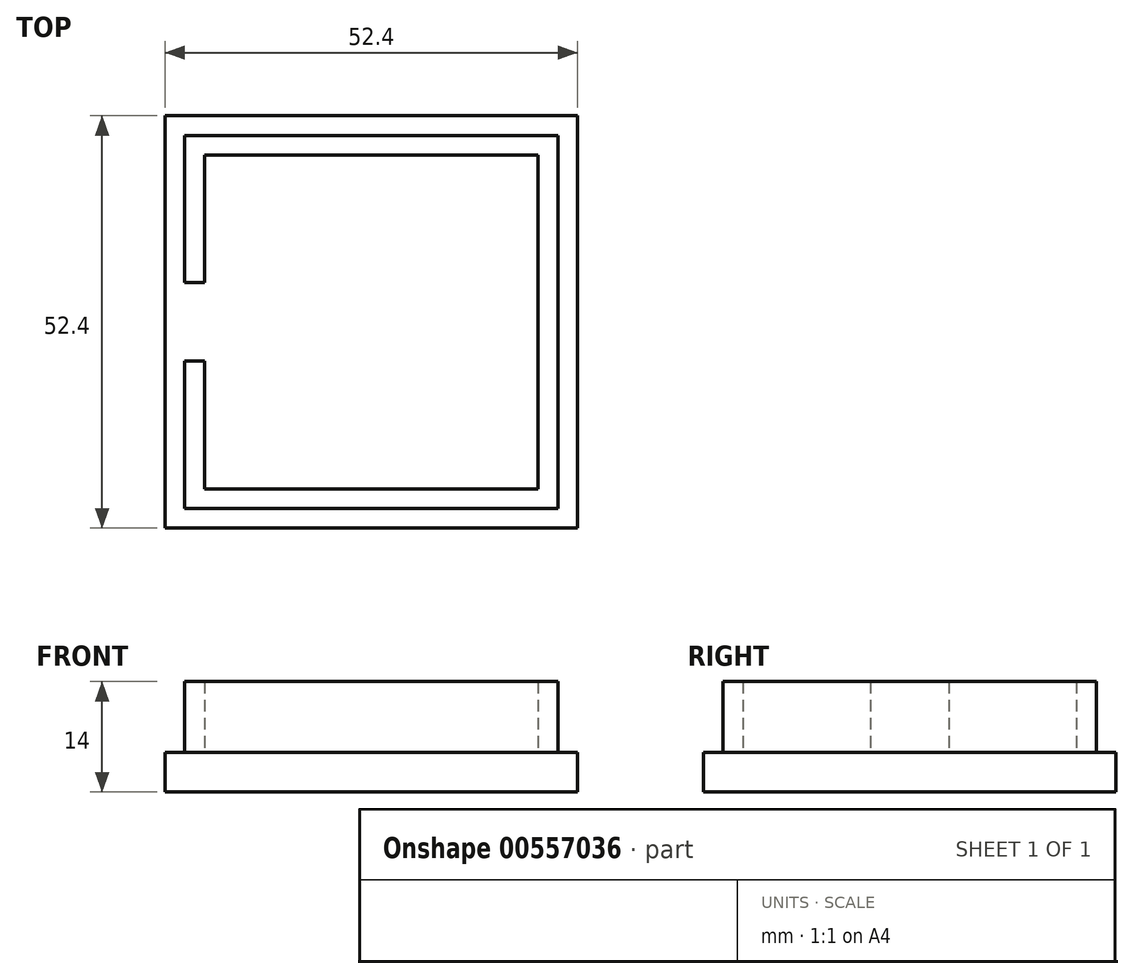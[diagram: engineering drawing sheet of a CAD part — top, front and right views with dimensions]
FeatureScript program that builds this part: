
annotation { "Feature Type Name" : "Feature", "Feature Type Description" : "" }
export const myFeature = defineFeature(function(context is Context, id is Id, definition is map)
    precondition{}
    {
        {
            var Q0;
            Q0=qCreatedBy(makeId("Top.planeOp"),FACE);
            var sketch = newSketch(context, id + "F0", { "sketchPlane" : qUnion([Q0])});
            skLineSegment(sketch, "E0.bottom", {"start": v(21.2, 21.2) * mm, "end": v(-21.2, 21.2) * mm});
            skLineSegment(sketch, "E0.top", {"start": v(21.2, -21.2) * mm, "end": v(-21.2, -21.2) * mm});
            skLineSegment(sketch, "E0.left", {"start": v(21.2, 21.2) * mm, "end": v(21.2, -21.2) * mm});
            skLineSegment(sketch, "E0.right", {"start": v(-21.2, 21.2) * mm, "end": v(-21.2, -21.2) * mm});
            skPoint(sketch, "E0.middle", {"position": v(0, 0) * mm});
            skLineSegment(sketch, "E1.bottom", {"start": v(23.7, 23.7) * mm, "end": v(-23.7, 23.7) * mm});
            skLineSegment(sketch, "E1.top", {"start": v(23.7, -23.7) * mm, "end": v(-23.7, -23.7) * mm});
            skLineSegment(sketch, "E1.left", {"start": v(23.7, 23.7) * mm, "end": v(23.7, -23.7) * mm});
            skLineSegment(sketch, "E1.right", {"start": v(-23.7, 23.7) * mm, "end": v(-23.7, -23.7) * mm});
            skLineSegment(sketch, "E2", {"start": v(0, 0) * mm, "end": v(-23.7, 0) * mm});
            skLineSegment(sketch, "E3", {"start": v(-23.7, 0) * mm, "end": v(-23.7, 5) * mm});
            skLineSegment(sketch, "E4", {"start": v(-21.2, 0) * mm, "end": v(-21.2, -5) * mm});
            skLineSegment(sketch, "E5.bottom", {"start": v(-23.7, 5) * mm, "end": v(-21.2, 5) * mm});
            skLineSegment(sketch, "E5.top", {"start": v(-23.7, -5) * mm, "end": v(-21.2, -5) * mm});
            skLineSegment(sketch, "E5.left", {"start": v(-23.7, 5) * mm, "end": v(-23.7, -5) * mm});
            skLineSegment(sketch, "E5.right", {"start": v(-21.2, 5) * mm, "end": v(-21.2, -5) * mm});
            skSolve(sketch);
        }
        {
            var Q0;
            {var subQ9=sQuery(id+"F0.wireOp",EDGE,"E0.bottom");Q0=makeQuery(id+"F0.imprint","IMPRINT",FACE,{"disambiguationData":[TD([[makeQuery(id+"F0.imprint","IMPRINT",EDGE,{"derivedFrom":subQ9}),-1.0]])]});}
            extrude(context, id + "F1", {"entities" : qUnion([Q0]), "depth" : 9 * mm, "offsetDistance" : 25 * mm});
        }
        {
            var Q0;
            Q0=qCreatedBy(makeId("Top.planeOp"),FACE);
            var sketch = newSketch(context, id + "F2", { "sketchPlane" : qUnion([Q0])});
            skLineSegment(sketch, "E6.bottom", {"start": v(-26.2, -26.2) * mm, "end": v(26.2, -26.2) * mm});
            skLineSegment(sketch, "E6.top", {"start": v(-26.2, 26.2) * mm, "end": v(26.2, 26.2) * mm});
            skLineSegment(sketch, "E6.left", {"start": v(-26.2, -26.2) * mm, "end": v(-26.2, 26.2) * mm});
            skLineSegment(sketch, "E6.right", {"start": v(26.2, -26.2) * mm, "end": v(26.2, 26.2) * mm});
            skPoint(sketch, "E6.middle", {"position": v(0, 0) * mm});
            skSolve(sketch);
        }
        {
            var Q0;
            Q0=makeQuery(id+"F2.imprint","IMPRINT",FACE,{"disambiguationData":[TD([[makeQuery(id+"F2.imprint","IMPRINT",EDGE,{"derivedFrom":sQuery(id+"F2.wireOp",EDGE,"E6.bottom")}),1.0]])]});
            extrude(context, id + "F3", {"entities" : qUnion([Q0]), "operationType" : NewBodyOperationType.ADD, "oppositeDirection" : true, "depth" : 5 * mm, "offsetDistance" : 25 * mm});
        }
    });
